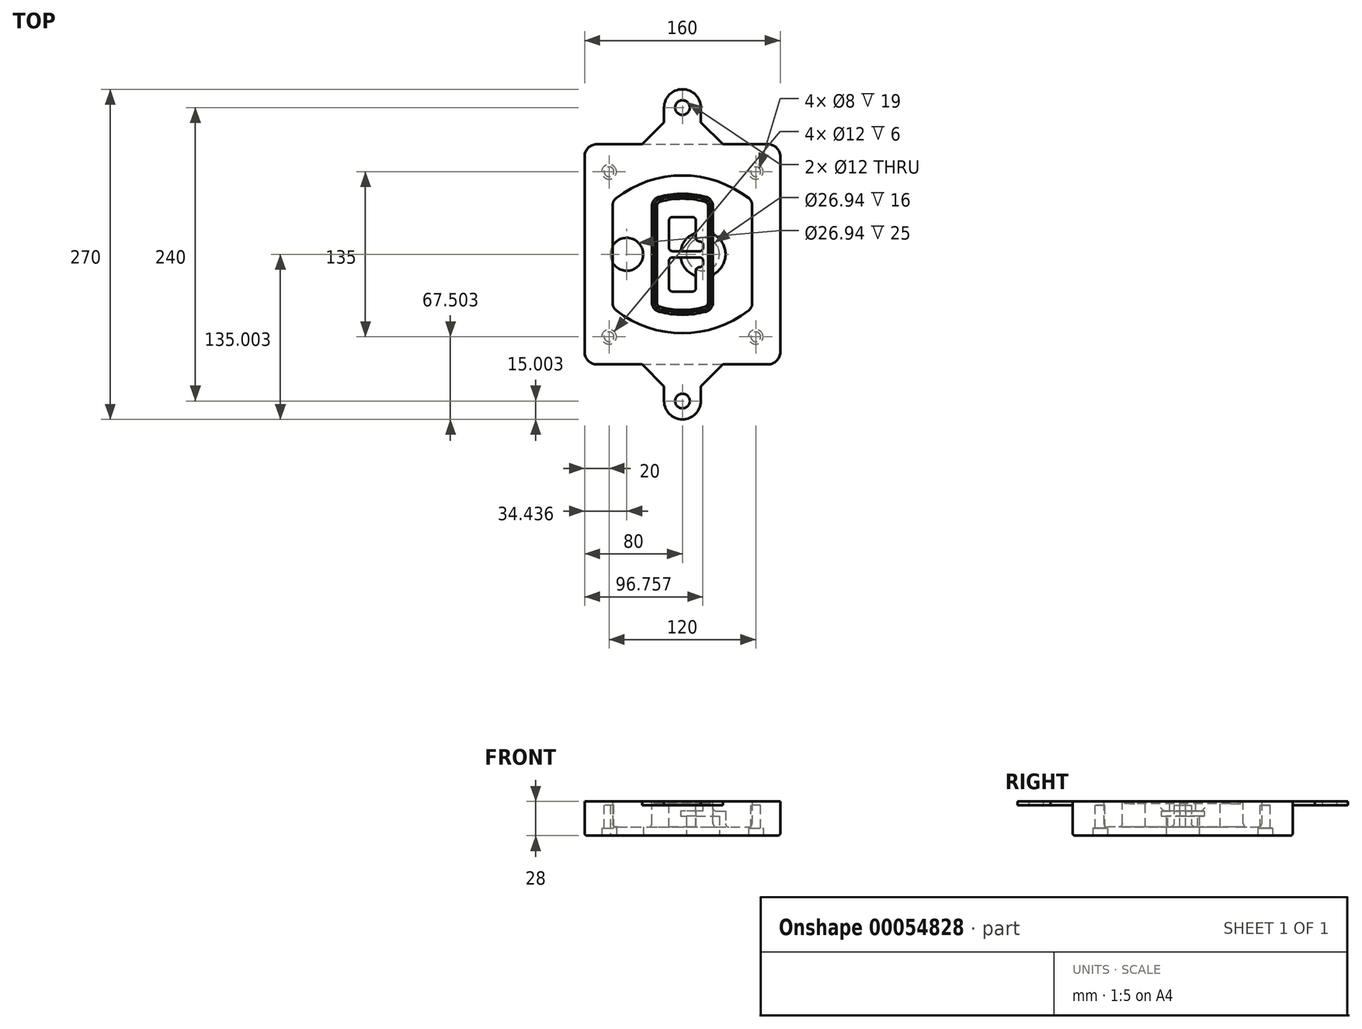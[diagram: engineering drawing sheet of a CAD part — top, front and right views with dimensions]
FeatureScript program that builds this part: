
annotation { "Feature Type Name" : "Feature", "Feature Type Description" : "" }
export const myFeature = defineFeature(function(context is Context, id is Id, definition is map)
    precondition{}
    {
        {
            var Q0;
            Q0=qCreatedBy(makeId("Top.planeOp"),FACE);
            var sketch = newSketch(context, id + "F0", { "sketchPlane" : qUnion([Q0])});
            skPoint(sketch, "E0.rect.middle", {"position": v(0, 0) * mm});
            skLineSegment(sketch, "E1.bottom", {"start": v(24.05, 28.38) * mm, "end": v(164.05, 28.38) * mm});
            skLineSegment(sketch, "E1.top", {"start": v(24.05, 208.38) * mm, "end": v(164.05, 208.38) * mm});
            skLineSegment(sketch, "E1.left", {"start": v(14.05, 38.38) * mm, "end": v(14.05, 198.38) * mm});
            skLineSegment(sketch, "E1.right", {"start": v(174.05, 38.38) * mm, "end": v(174.05, 198.38) * mm});
            skLineSegment(sketch, "E2", {"start": v(14.05, 208.38) * mm, "end": v(174.05, 28.38) * mm, "construction": true});
            skLineSegment(sketch, "E3", {"start": v(174.05, 208.38) * mm, "end": v(14.05, 28.38) * mm, "construction": true});
            skCircle(sketch, "E4", {"center": v(34.05, 185.88) * mm, "radius": 4 * mm});
            skCircle(sketch, "E5", {"center": v(154.05, 185.88) * mm, "radius": 4 * mm});
            skCircle(sketch, "E6", {"center": v(154.05, 50.88) * mm, "radius": 4 * mm});
            skCircle(sketch, "E7", {"center": v(34.05, 50.88) * mm, "radius": 4 * mm});
            skLineSegment(sketch, "E8", {"start": v(34.05, 185.88) * mm, "end": v(154.05, 185.88) * mm, "construction": true});
            skLineSegment(sketch, "E9", {"start": v(154.05, 185.88) * mm, "end": v(154.05, 50.88) * mm, "construction": true});
            skLineSegment(sketch, "E10", {"start": v(154.05, 50.88) * mm, "end": v(34.05, 50.88) * mm, "construction": true});
            skLineSegment(sketch, "E11", {"start": v(34.05, 50.88) * mm, "end": v(34.05, 185.88) * mm, "construction": true});
            skLineSegment(sketch, "E12", {"start": v(34.05, 158.68) * mm, "end": v(34.05, 78.09) * mm});
            skLineSegment(sketch, "E13", {"start": v(154.05, 158.68) * mm, "end": v(154.05, 78.09) * mm});
            skArc(sketch, "E14", {"start": v(150.2, 166.56) * mm, "mid": v(94.05, 185.88) * mm, "end": v(37.9, 166.56) * mm});
            skArc(sketch, "E15", {"start": v(37.9, 70.2) * mm, "mid": v(94.05, 50.88) * mm, "end": v(150.2, 70.2) * mm});
            skLineSegment(sketch, "E16", {"start": v(34.05, 118.38) * mm, "end": v(154.05, 118.38) * mm, "construction": true});
            skPoint(sketch, "E17.visualSharp", {"position": v(34.05, 73.38) * mm});
            skArc(sketch, "E17.filletArc", {"start": v(34.05, 78.09) * mm, "mid": v(35.06, 73.7) * mm, "end": v(37.9, 70.2) * mm});
            skPoint(sketch, "E18.visualSharp", {"position": v(34.05, 163.38) * mm});
            skArc(sketch, "E18.filletArc", {"start": v(37.9, 166.56) * mm, "mid": v(35.06, 163.06) * mm, "end": v(34.05, 158.68) * mm});
            skPoint(sketch, "E19.visualSharp", {"position": v(154.05, 163.38) * mm});
            skArc(sketch, "E19.filletArc", {"start": v(154.05, 158.68) * mm, "mid": v(153.04, 163.06) * mm, "end": v(150.2, 166.56) * mm});
            skPoint(sketch, "E20.visualSharp", {"position": v(154.05, 73.38) * mm});
            skArc(sketch, "E20.filletArc", {"start": v(150.2, 70.2) * mm, "mid": v(153.04, 73.7) * mm, "end": v(154.05, 78.09) * mm});
            skPoint(sketch, "E21.visualSharp", {"position": v(14.05, 208.38) * mm});
            skArc(sketch, "E21.filletArc", {"start": v(24.05, 208.38) * mm, "mid": v(16.98, 205.45) * mm, "end": v(14.05, 198.38) * mm});
            skPoint(sketch, "E22.visualSharp", {"position": v(174.05, 208.38) * mm});
            skArc(sketch, "E22.filletArc", {"start": v(174.05, 198.38) * mm, "mid": v(171.12, 205.45) * mm, "end": v(164.05, 208.38) * mm});
            skPoint(sketch, "E23.visualSharp", {"position": v(174.05, 28.38) * mm});
            skArc(sketch, "E23.filletArc", {"start": v(164.05, 28.38) * mm, "mid": v(171.12, 31.31) * mm, "end": v(174.05, 38.38) * mm});
            skPoint(sketch, "E24.visualSharp", {"position": v(14.05, 28.38) * mm});
            skArc(sketch, "E24.filletArc", {"start": v(14.05, 38.38) * mm, "mid": v(16.98, 31.31) * mm, "end": v(24.05, 28.38) * mm});
            skArc(sketch, "E25.0", {"start": v(151.05, 158.68) * mm, "mid": v(150.34, 161.75) * mm, "end": v(148.36, 164.2) * mm});
            skLineSegment(sketch, "E25.1", {"start": v(151.05, 158.68) * mm, "end": v(151.05, 78.09) * mm});
            skArc(sketch, "E25.2", {"start": v(148.36, 72.57) * mm, "mid": v(150.34, 75.02) * mm, "end": v(151.05, 78.09) * mm});
            skArc(sketch, "E25.3", {"start": v(39.74, 72.57) * mm, "mid": v(94.05, 53.88) * mm, "end": v(148.36, 72.57) * mm});
            skArc(sketch, "E25.4", {"start": v(37.05, 78.09) * mm, "mid": v(37.76, 75.02) * mm, "end": v(39.74, 72.57) * mm});
            skArc(sketch, "E25.5", {"start": v(148.36, 164.2) * mm, "mid": v(94.05, 182.88) * mm, "end": v(39.74, 164.2) * mm});
            skLineSegment(sketch, "E25.6", {"start": v(37.05, 158.68) * mm, "end": v(37.05, 78.09) * mm});
            skArc(sketch, "E25.7", {"start": v(39.74, 164.2) * mm, "mid": v(37.76, 161.75) * mm, "end": v(37.05, 158.68) * mm});
            skArc(sketch, "E26.0", {"start": v(35.43, 169.71) * mm, "mid": v(31.47, 164.82) * mm, "end": v(30.05, 158.68) * mm});
            skArc(sketch, "E26.1", {"start": v(152.67, 169.71) * mm, "mid": v(94.05, 189.88) * mm, "end": v(35.43, 169.71) * mm});
            skArc(sketch, "E26.2", {"start": v(158.05, 158.68) * mm, "mid": v(156.63, 164.82) * mm, "end": v(152.67, 169.71) * mm});
            skLineSegment(sketch, "E26.3", {"start": v(158.05, 158.68) * mm, "end": v(158.05, 78.09) * mm});
            skArc(sketch, "E26.4", {"start": v(152.67, 67.05) * mm, "mid": v(156.63, 71.95) * mm, "end": v(158.05, 78.09) * mm});
            skLineSegment(sketch, "E26.5", {"start": v(30.05, 158.68) * mm, "end": v(30.05, 78.09) * mm});
            skArc(sketch, "E26.6", {"start": v(35.43, 67.05) * mm, "mid": v(94.05, 46.88) * mm, "end": v(152.67, 67.05) * mm});
            skArc(sketch, "E26.7", {"start": v(30.05, 78.09) * mm, "mid": v(31.47, 71.95) * mm, "end": v(35.43, 67.05) * mm});
            skSolve(sketch);
        }
        {
            var Q0;
            Q0=makeQuery(id+"F0.imprint","IMPRINT",FACE,{"disambiguationData":[TD([[makeQuery(id+"F0.imprint","IMPRINT",EDGE,{"derivedFrom":sQuery(id+"F0.wireOp",EDGE,"E1.bottom")}),1.0]])]});
            var Q1;
            Q1=makeQuery(id+"F0.imprint","IMPRINT",FACE,{"disambiguationData":[TD([[makeQuery(id+"F0.imprint","IMPRINT",EDGE,{"derivedFrom":sQuery(id+"F0.wireOp",EDGE,"E12")}),1.0]])]});
            var Q2;
            Q2=makeQuery(id+"F0.imprint","IMPRINT",FACE,{"disambiguationData":[TD([[makeQuery(id+"F0.imprint","IMPRINT",EDGE,{"derivedFrom":sQuery(id+"F0.wireOp",EDGE,"E25.0")}),1.0]])]});
            var Q3;
            Q3=makeQuery(id+"F0.imprint","IMPRINT",FACE,{"disambiguationData":[TD([[makeQuery(id+"F0.imprint","IMPRINT",EDGE,{"derivedFrom":sQuery(id+"F0.wireOp",EDGE,"E12")}),-1.0]])]});
            extrude(context, id + "F1", {"entities" : qUnion([Q0, Q1, Q2, Q3]), "oppositeDirection" : true, "depth" : 25 * mm});
        }
        {
            var Q0;
            Q0=makeQuery(id+"F0.imprint","IMPRINT",FACE,{"disambiguationData":[TD([[makeQuery(id+"F0.imprint","IMPRINT",EDGE,{"derivedFrom":sQuery(id+"F0.wireOp",EDGE,"E12")}),1.0]])]});
            extrude(context, id + "F2", {"entities" : qUnion([Q0]), "operationType" : NewBodyOperationType.ADD, "depth" : 3 * mm});
        }
        {
            var Q0;
            Q0=makeQuery(id+"F0.imprint","IMPRINT",FACE,{"disambiguationData":[TD([[makeQuery(id+"F0.imprint","IMPRINT",EDGE,{"derivedFrom":sQuery(id+"F0.wireOp",EDGE,"E25.0")}),1.0]])]});
            extrude(context, id + "F3", {"entities" : qUnion([Q0]), "operationType" : NewBodyOperationType.REMOVE, "oppositeDirection" : true, "depth" : 18 * mm});
        }
        {
            var Q0;
            Q0=makeQuery(id+"F2.opExtrude","CAP_FACE",FACE,{"disambiguationData":[OSD([sQuery(id+"F0.wireOp",EDGE,"E12"),sQuery(id+"F0.wireOp",EDGE,"E13"),sQuery(id+"F0.wireOp",EDGE,"E14"),sQuery(id+"F0.wireOp",EDGE,"E15"),sQuery(id+"F0.wireOp",EDGE,"E17.filletArc"),sQuery(id+"F0.wireOp",EDGE,"E18.filletArc"),sQuery(id+"F0.wireOp",EDGE,"E19.filletArc"),sQuery(id+"F0.wireOp",EDGE,"E20.filletArc"),sQuery(id+"F0.wireOp",EDGE,"E25.0"),sQuery(id+"F0.wireOp",EDGE,"E25.1"),sQuery(id+"F0.wireOp",EDGE,"E25.2"),sQuery(id+"F0.wireOp",EDGE,"E25.3"),sQuery(id+"F0.wireOp",EDGE,"E25.4"),sQuery(id+"F0.wireOp",EDGE,"E25.5"),sQuery(id+"F0.wireOp",EDGE,"E25.6"),sQuery(id+"F0.wireOp",EDGE,"E25.7")])],"isStart":false});
            var sketch = newSketch(context, id + "F4", { "sketchPlane" : qUnion([Q0])});
            skArc(sketch, "E27.0", {"start": v(74.97, 71.41) * mm, "mid": v(94.05, 68.88) * mm, "end": v(113.13, 71.41) * mm});
            skArc(sketch, "E28.0", {"start": v(113.13, 165.35) * mm, "mid": v(94.05, 167.88) * mm, "end": v(74.97, 165.35) * mm});
            skLineSegment(sketch, "E29", {"start": v(69.05, 157.63) * mm, "end": v(69.05, 79.14) * mm});
            skLineSegment(sketch, "E30", {"start": v(119.05, 157.63) * mm, "end": v(119.05, 79.14) * mm});
            skLineSegment(sketch, "E31", {"start": v(69.05, 163.48) * mm, "end": v(119.05, 163.48) * mm, "construction": true});
            skLineSegment(sketch, "E32", {"start": v(69.05, 73.28) * mm, "end": v(119.05, 73.28) * mm, "construction": true});
            skPoint(sketch, "E33.visualSharp", {"position": v(69.05, 163.48) * mm});
            skArc(sketch, "E33.filletArc", {"start": v(74.97, 165.35) * mm, "mid": v(70.7, 162.5) * mm, "end": v(69.05, 157.63) * mm});
            skPoint(sketch, "E34.visualSharp", {"position": v(119.05, 163.48) * mm});
            skArc(sketch, "E34.filletArc", {"start": v(119.05, 157.63) * mm, "mid": v(117.4, 162.5) * mm, "end": v(113.13, 165.35) * mm});
            skPoint(sketch, "E35.visualSharp", {"position": v(119.05, 73.28) * mm});
            skArc(sketch, "E35.filletArc", {"start": v(113.13, 71.41) * mm, "mid": v(117.4, 74.27) * mm, "end": v(119.05, 79.14) * mm});
            skPoint(sketch, "E36.visualSharp", {"position": v(69.05, 73.28) * mm});
            skArc(sketch, "E36.filletArc", {"start": v(69.05, 79.14) * mm, "mid": v(70.7, 74.27) * mm, "end": v(74.97, 71.41) * mm});
            skArc(sketch, "E37.0", {"start": v(148.36, 164.2) * mm, "mid": v(94.05, 182.88) * mm, "end": v(39.74, 164.2) * mm});
            skArc(sketch, "E37.1", {"start": v(39.74, 164.2) * mm, "mid": v(37.76, 161.75) * mm, "end": v(37.05, 158.68) * mm});
            skLineSegment(sketch, "E37.2", {"start": v(37.05, 158.68) * mm, "end": v(37.05, 78.09) * mm});
            skArc(sketch, "E37.3", {"start": v(37.05, 78.09) * mm, "mid": v(37.76, 75.02) * mm, "end": v(39.74, 72.57) * mm});
            skArc(sketch, "E37.4", {"start": v(39.74, 72.57) * mm, "mid": v(94.05, 53.88) * mm, "end": v(148.36, 72.57) * mm});
            skArc(sketch, "E37.5", {"start": v(148.36, 72.57) * mm, "mid": v(150.34, 75.02) * mm, "end": v(151.05, 78.09) * mm});
            skLineSegment(sketch, "E37.6", {"start": v(151.05, 158.68) * mm, "end": v(151.05, 78.09) * mm});
            skArc(sketch, "E37.7", {"start": v(151.05, 158.68) * mm, "mid": v(150.34, 161.75) * mm, "end": v(148.36, 164.2) * mm});
            skLineSegment(sketch, "E38.0", {"start": v(117.05, 157.63) * mm, "end": v(117.05, 79.14) * mm});
            skArc(sketch, "E38.1", {"start": v(112.61, 73.34) * mm, "mid": v(115.81, 75.49) * mm, "end": v(117.05, 79.14) * mm});
            skArc(sketch, "E38.2", {"start": v(75.49, 73.34) * mm, "mid": v(94.05, 70.88) * mm, "end": v(112.61, 73.34) * mm});
            skArc(sketch, "E38.3", {"start": v(71.05, 79.14) * mm, "mid": v(72.29, 75.49) * mm, "end": v(75.49, 73.34) * mm});
            skLineSegment(sketch, "E38.4", {"start": v(71.05, 157.63) * mm, "end": v(71.05, 79.14) * mm});
            skArc(sketch, "E38.5", {"start": v(117.05, 157.63) * mm, "mid": v(115.81, 161.28) * mm, "end": v(112.61, 163.42) * mm});
            skArc(sketch, "E38.6", {"start": v(75.49, 163.42) * mm, "mid": v(72.29, 161.28) * mm, "end": v(71.05, 157.63) * mm});
            skArc(sketch, "E38.7", {"start": v(112.61, 163.42) * mm, "mid": v(94.05, 165.88) * mm, "end": v(75.49, 163.42) * mm});
            skArc(sketch, "E39.0", {"start": v(115.05, 157.63) * mm, "mid": v(114.23, 160.06) * mm, "end": v(112.1, 161.5) * mm});
            skLineSegment(sketch, "E39.1", {"start": v(115.05, 157.63) * mm, "end": v(115.05, 79.14) * mm});
            skArc(sketch, "E39.2", {"start": v(112.1, 75.27) * mm, "mid": v(114.23, 76.7) * mm, "end": v(115.05, 79.14) * mm});
            skArc(sketch, "E39.3", {"start": v(76, 75.27) * mm, "mid": v(94.05, 72.88) * mm, "end": v(112.1, 75.27) * mm});
            skArc(sketch, "E39.4", {"start": v(73.05, 79.14) * mm, "mid": v(73.87, 76.7) * mm, "end": v(76, 75.27) * mm});
            skArc(sketch, "E39.5", {"start": v(112.1, 161.5) * mm, "mid": v(94.05, 163.88) * mm, "end": v(76, 161.5) * mm});
            skLineSegment(sketch, "E39.6", {"start": v(73.05, 157.63) * mm, "end": v(73.05, 79.14) * mm});
            skArc(sketch, "E39.7", {"start": v(76, 161.5) * mm, "mid": v(73.87, 160.06) * mm, "end": v(73.05, 157.63) * mm});
            skLineSegment(sketch, "E40", {"start": v(69.05, 118.38) * mm, "end": v(119.05, 118.38) * mm, "construction": true});
            skLineSegment(sketch, "E41", {"start": v(83.05, 123.88) * mm, "end": v(83.05, 145.88) * mm});
            skLineSegment(sketch, "E42", {"start": v(86.05, 148.88) * mm, "end": v(102.05, 148.88) * mm});
            skLineSegment(sketch, "E43", {"start": v(105.05, 145.88) * mm, "end": v(105.05, 131.88) * mm});
            skLineSegment(sketch, "E44", {"start": v(108.05, 128.88) * mm, "end": v(108.05, 128.88) * mm});
            skLineSegment(sketch, "E45", {"start": v(111.05, 125.88) * mm, "end": v(111.05, 123.88) * mm});
            skLineSegment(sketch, "E46", {"start": v(108.05, 120.88) * mm, "end": v(86.05, 120.88) * mm});
            skPoint(sketch, "E47.visualSharp", {"position": v(83.05, 148.88) * mm});
            skArc(sketch, "E47.filletArc", {"start": v(86.05, 148.88) * mm, "mid": v(83.93, 148) * mm, "end": v(83.05, 145.88) * mm});
            skPoint(sketch, "E48.visualSharp", {"position": v(105.05, 148.88) * mm});
            skArc(sketch, "E48.filletArc", {"start": v(105.05, 145.88) * mm, "mid": v(104.17, 148) * mm, "end": v(102.05, 148.88) * mm});
            skPoint(sketch, "E49.visualSharp", {"position": v(105.05, 128.88) * mm});
            skArc(sketch, "E49.filletArc", {"start": v(105.05, 131.88) * mm, "mid": v(105.93, 129.76) * mm, "end": v(108.05, 128.88) * mm});
            skPoint(sketch, "E50.visualSharp", {"position": v(111.05, 128.88) * mm});
            skArc(sketch, "E50.filletArc", {"start": v(111.05, 125.88) * mm, "mid": v(110.17, 128) * mm, "end": v(108.05, 128.88) * mm});
            skPoint(sketch, "E51.visualSharp", {"position": v(111.05, 120.88) * mm});
            skArc(sketch, "E51.filletArc", {"start": v(108.05, 120.88) * mm, "mid": v(110.17, 121.76) * mm, "end": v(111.05, 123.88) * mm});
            skPoint(sketch, "E52.visualSharp", {"position": v(83.05, 120.88) * mm});
            skArc(sketch, "E52.filletArc", {"start": v(83.05, 123.88) * mm, "mid": v(83.93, 121.76) * mm, "end": v(86.05, 120.88) * mm});
            skLineSegment(sketch, "E53.0.MirrorCS", {"start": v(108.05, 115.88) * mm, "end": v(86.05, 115.88) * mm});
            skArc(sketch, "E54.0.MirrorCS", {"start": v(83.05, 112.88) * mm, "mid": v(83.93, 115) * mm, "end": v(86.05, 115.88) * mm});
            skLineSegment(sketch, "E55.0.MirrorCS", {"start": v(83.05, 112.88) * mm, "end": v(83.05, 90.88) * mm});
            skArc(sketch, "E56.0.MirrorCS", {"start": v(86.05, 87.88) * mm, "mid": v(83.93, 88.76) * mm, "end": v(83.05, 90.88) * mm});
            skLineSegment(sketch, "E57.0.MirrorCS", {"start": v(86.05, 87.88) * mm, "end": v(102.05, 87.88) * mm});
            skArc(sketch, "E58.0.MirrorCS", {"start": v(105.05, 90.88) * mm, "mid": v(104.17, 88.76) * mm, "end": v(102.05, 87.88) * mm});
            skLineSegment(sketch, "E59.0.MirrorCS", {"start": v(105.05, 90.88) * mm, "end": v(105.05, 104.88) * mm});
            skArc(sketch, "E60.0.MirrorCS", {"start": v(105.05, 104.88) * mm, "mid": v(105.93, 107) * mm, "end": v(108.05, 107.88) * mm});
            skArc(sketch, "E61.0.MirrorCS", {"start": v(111.05, 110.88) * mm, "mid": v(110.17, 108.76) * mm, "end": v(108.05, 107.88) * mm});
            skLineSegment(sketch, "E62.0.MirrorCS", {"start": v(111.05, 110.88) * mm, "end": v(111.05, 112.88) * mm});
            skArc(sketch, "E63.0.MirrorCS", {"start": v(108.05, 115.88) * mm, "mid": v(110.17, 115) * mm, "end": v(111.05, 112.88) * mm});
            skSolve(sketch);
        }
        {
            var Q0;
            Q0=makeQuery(id+"F4.imprint","IMPRINT",FACE,{"disambiguationData":[TD([[makeQuery(id+"F4.imprint","IMPRINT",EDGE,{"derivedFrom":sQuery(id+"F4.wireOp",EDGE,"E27.0")}),1.0]])]});
            var Q1;
            Q1=makeQuery(id+"F4.imprint","IMPRINT",FACE,{"disambiguationData":[TD([[makeQuery(id+"F4.imprint","IMPRINT",EDGE,{"derivedFrom":sQuery(id+"F4.wireOp",EDGE,"E38.0")}),-1.0]])]});
            var Q2;
            Q2=makeQuery(id+"F4.imprint","IMPRINT",FACE,{"disambiguationData":[TD([[makeQuery(id+"F4.imprint","IMPRINT",EDGE,{"derivedFrom":sQuery(id+"F4.wireOp",EDGE,"E39.0")}),1.0]])]});
            extrude(context, id + "F5", {"entities" : qUnion([Q0, Q1, Q2]), "operationType" : NewBodyOperationType.ADD, "endBound" : BoundingType.UP_TO_NEXT, "oppositeDirection" : true, "depth" : 25 * mm});
        }
        {
            var Q0;
            Q0=makeQuery(id+"F4.imprint","IMPRINT",FACE,{"disambiguationData":[TD([[makeQuery(id+"F4.imprint","IMPRINT",EDGE,{"derivedFrom":sQuery(id+"F4.wireOp",EDGE,"E38.0")}),-1.0]])]});
            extrude(context, id + "F6", {"entities" : qUnion([Q0]), "operationType" : NewBodyOperationType.REMOVE, "oppositeDirection" : true, "depth" : 2 * mm});
        }
        {
            var Q0;
            Q0=makeQuery(id+"F1.opExtrude","CAP_FACE",FACE,{"disambiguationData":[OSD([sQuery(id+"F0.wireOp",EDGE,"E1.bottom"),sQuery(id+"F0.wireOp",EDGE,"E1.top"),sQuery(id+"F0.wireOp",EDGE,"E1.left"),sQuery(id+"F0.wireOp",EDGE,"E1.right"),sQuery(id+"F0.wireOp",EDGE,"E4"),sQuery(id+"F0.wireOp",EDGE,"E5"),sQuery(id+"F0.wireOp",EDGE,"E6"),sQuery(id+"F0.wireOp",EDGE,"E7"),sQuery(id+"F0.wireOp",EDGE,"E21.filletArc"),sQuery(id+"F0.wireOp",EDGE,"E22.filletArc"),sQuery(id+"F0.wireOp",EDGE,"E23.filletArc"),sQuery(id+"F0.wireOp",EDGE,"E24.filletArc")])],"isStart":false});
            var sketch = newSketch(context, id + "F7", { "sketchPlane" : qUnion([Q0])});
            skCircle(sketch, "E64", {"center": v(110.8, -118.38) * mm, "radius": 13.47 * mm});
            skCircle(sketch, "E65", {"center": v(48.49, -118.38) * mm, "radius": 13.47 * mm});
            skLineSegment(sketch, "E66", {"start": v(174.05, -118.38) * mm, "end": v(14.05, -118.38) * mm});
            skCircle(sketch, "E67", {"center": v(110.8, -118.38) * mm, "radius": 18.47 * mm});
            skCircle(sketch, "E68", {"center": v(154.05, -185.88) * mm, "radius": 6 * mm});
            skCircle(sketch, "E69", {"center": v(34.05, -185.88) * mm, "radius": 6 * mm});
            skCircle(sketch, "E70", {"center": v(34.05, -50.88) * mm, "radius": 6 * mm});
            skCircle(sketch, "E71", {"center": v(154.05, -50.88) * mm, "radius": 6 * mm});
            skSolve(sketch);
        }
        {
            var Q0;
            {var subQ1=sQuery(id+"F7.wireOp",EDGE,"E66");var subQ4=sQuery(id+"F7.wireOp",EDGE,"E64");var subQ6=makeQuery(id+"F7.imprint","INTERSECT",VERTEX,{"disambiguationData":[OD(0.0)],"derivedFrom":[subQ4,subQ1]});Q0=makeQuery(id+"F7.imprint","IMPRINT",FACE,{"disambiguationData":[TD([[makeQuery(id+"F7.imprint","IMPRINT",EDGE,{"disambiguationData":[TD([[subQ6,-1.0]])],"derivedFrom":subQ4}),-1.0]])]});}
            var Q1;
            {var subQ0=sQuery(id+"F7.wireOp",EDGE,"E66");var subQ1=sQuery(id+"F7.wireOp",EDGE,"E64");var subQ3=makeQuery(id+"F7.imprint","INTERSECT",VERTEX,{"disambiguationData":[OD(0.0)],"derivedFrom":[subQ1,subQ0]});Q1=makeQuery(id+"F7.imprint","IMPRINT",FACE,{"disambiguationData":[TD([[makeQuery(id+"F7.imprint","IMPRINT",EDGE,{"disambiguationData":[TD([[subQ3,-1.0]])],"derivedFrom":subQ1}),1.0]])]});}
            var Q2;
            {var subQ0=sQuery(id+"F7.wireOp",EDGE,"E66");var subQ1=sQuery(id+"F7.wireOp",EDGE,"E64");var subQ3=makeQuery(id+"F7.imprint","INTERSECT",VERTEX,{"disambiguationData":[OD(0.0)],"derivedFrom":[subQ1,subQ0]});Q2=makeQuery(id+"F7.imprint","IMPRINT",FACE,{"disambiguationData":[TD([[makeQuery(id+"F7.imprint","IMPRINT",EDGE,{"disambiguationData":[TD([[subQ3,1.0]])],"derivedFrom":subQ1}),1.0]])]});}
            var Q3;
            {var subQ1=sQuery(id+"F7.wireOp",EDGE,"E66");var subQ4=sQuery(id+"F7.wireOp",EDGE,"E64");var subQ6=makeQuery(id+"F7.imprint","INTERSECT",VERTEX,{"disambiguationData":[OD(0.0)],"derivedFrom":[subQ4,subQ1]});Q3=makeQuery(id+"F7.imprint","IMPRINT",FACE,{"disambiguationData":[TD([[makeQuery(id+"F7.imprint","IMPRINT",EDGE,{"disambiguationData":[TD([[subQ6,1.0]])],"derivedFrom":subQ4}),-1.0]])]});}
            extrude(context, id + "F8", {"entities" : qUnion([Q0, Q1, Q2, Q3]), "operationType" : NewBodyOperationType.ADD, "oppositeDirection" : true, "depth" : 20 * mm});
        }
        {
            var Q0;
            {var subQ0=sQuery(id+"F7.wireOp",EDGE,"E66");var subQ1=sQuery(id+"F7.wireOp",EDGE,"E64");var subQ3=makeQuery(id+"F7.imprint","INTERSECT",VERTEX,{"disambiguationData":[OD(0.0)],"derivedFrom":[subQ1,subQ0]});Q0=makeQuery(id+"F7.imprint","IMPRINT",FACE,{"disambiguationData":[TD([[makeQuery(id+"F7.imprint","IMPRINT",EDGE,{"disambiguationData":[TD([[subQ3,-1.0]])],"derivedFrom":subQ1}),1.0]])]});}
            var Q1;
            {var subQ0=sQuery(id+"F7.wireOp",EDGE,"E66");var subQ1=sQuery(id+"F7.wireOp",EDGE,"E64");var subQ3=makeQuery(id+"F7.imprint","INTERSECT",VERTEX,{"disambiguationData":[OD(0.0)],"derivedFrom":[subQ1,subQ0]});Q1=makeQuery(id+"F7.imprint","IMPRINT",FACE,{"disambiguationData":[TD([[makeQuery(id+"F7.imprint","IMPRINT",EDGE,{"disambiguationData":[TD([[subQ3,1.0]])],"derivedFrom":subQ1}),1.0]])]});}
            extrude(context, id + "F9", {"entities" : qUnion([Q0, Q1]), "operationType" : NewBodyOperationType.REMOVE, "oppositeDirection" : true, "depth" : 16 * mm});
        }
        {
            var Q0;
            {var subQ0=sQuery(id+"F7.wireOp",EDGE,"E66");var subQ1=sQuery(id+"F7.wireOp",EDGE,"E65");var subQ3=makeQuery(id+"F7.imprint","INTERSECT",VERTEX,{"disambiguationData":[OD(0.0)],"derivedFrom":[subQ1,subQ0]});Q0=makeQuery(id+"F7.imprint","IMPRINT",FACE,{"disambiguationData":[TD([[makeQuery(id+"F7.imprint","IMPRINT",EDGE,{"disambiguationData":[TD([[subQ3,-1.0]])],"derivedFrom":subQ1}),1.0]])]});}
            var Q1;
            {var subQ0=sQuery(id+"F7.wireOp",EDGE,"E66");var subQ1=sQuery(id+"F7.wireOp",EDGE,"E65");var subQ3=makeQuery(id+"F7.imprint","INTERSECT",VERTEX,{"disambiguationData":[OD(0.0)],"derivedFrom":[subQ1,subQ0]});Q1=makeQuery(id+"F7.imprint","IMPRINT",FACE,{"disambiguationData":[TD([[makeQuery(id+"F7.imprint","IMPRINT",EDGE,{"disambiguationData":[TD([[subQ3,1.0]])],"derivedFrom":subQ1}),1.0]])]});}
            extrude(context, id + "F10", {"entities" : qUnion([Q0, Q1]), "operationType" : NewBodyOperationType.REMOVE, "oppositeDirection" : true, "depth" : 25 * mm});
        }
        {
            var Q0;
            Q0=makeQuery(id+"F7.imprint","IMPRINT",FACE,{"disambiguationData":[TD([[makeQuery(id+"F7.imprint","IMPRINT",EDGE,{"derivedFrom":sQuery(id+"F7.wireOp",EDGE,"E68")}),1.0]])]});
            var Q1;
            Q1=makeQuery(id+"F7.imprint","IMPRINT",FACE,{"disambiguationData":[TD([[makeQuery(id+"F7.imprint","IMPRINT",EDGE,{"derivedFrom":makeQuery(id+"F1.opExtrude","CAP_EDGE",EDGE,{"disambiguationData":[OSD([sQuery(id+"F0.wireOp",EDGE,"E5")])],"isStart":false})}),-1.0]])]});
            var Q2;
            Q2=makeQuery(id+"F7.imprint","IMPRINT",FACE,{"disambiguationData":[TD([[makeQuery(id+"F7.imprint","IMPRINT",EDGE,{"derivedFrom":sQuery(id+"F7.wireOp",EDGE,"E69")}),1.0]])]});
            var Q3;
            Q3=makeQuery(id+"F7.imprint","IMPRINT",FACE,{"disambiguationData":[TD([[makeQuery(id+"F7.imprint","IMPRINT",EDGE,{"derivedFrom":makeQuery(id+"F1.opExtrude","CAP_EDGE",EDGE,{"disambiguationData":[OSD([sQuery(id+"F0.wireOp",EDGE,"E4")])],"isStart":false})}),-1.0]])]});
            var Q4;
            Q4=makeQuery(id+"F7.imprint","IMPRINT",FACE,{"disambiguationData":[TD([[makeQuery(id+"F7.imprint","IMPRINT",EDGE,{"derivedFrom":sQuery(id+"F7.wireOp",EDGE,"E70")}),1.0]])]});
            var Q5;
            Q5=makeQuery(id+"F7.imprint","IMPRINT",FACE,{"disambiguationData":[TD([[makeQuery(id+"F7.imprint","IMPRINT",EDGE,{"derivedFrom":makeQuery(id+"F1.opExtrude","CAP_EDGE",EDGE,{"disambiguationData":[OSD([sQuery(id+"F0.wireOp",EDGE,"E7")])],"isStart":false})}),-1.0]])]});
            var Q6;
            Q6=makeQuery(id+"F7.imprint","IMPRINT",FACE,{"disambiguationData":[TD([[makeQuery(id+"F7.imprint","IMPRINT",EDGE,{"derivedFrom":sQuery(id+"F7.wireOp",EDGE,"E71")}),1.0]])]});
            var Q7;
            Q7=makeQuery(id+"F7.imprint","IMPRINT",FACE,{"disambiguationData":[TD([[makeQuery(id+"F7.imprint","IMPRINT",EDGE,{"derivedFrom":makeQuery(id+"F1.opExtrude","CAP_EDGE",EDGE,{"disambiguationData":[OSD([sQuery(id+"F0.wireOp",EDGE,"E6")])],"isStart":false})}),-1.0]])]});
            extrude(context, id + "F11", {"entities" : qUnion([Q0, Q1, Q2, Q3, Q4, Q5, Q6, Q7]), "operationType" : NewBodyOperationType.REMOVE, "oppositeDirection" : true, "depth" : 6 * mm});
        }
        {
            var Q0;
            Q0=makeQuery(id+"F9.boolean.opBoolean","COPY",FACE,{"derivedFrom":makeQuery(id+"F9.opExtrude","CAP_FACE",FACE,{"disambiguationData":[OSD([sQuery(id+"F7.wireOp",EDGE,"E64")])],"isStart":false})});
            var sketch = newSketch(context, id + "F12", { "sketchPlane" : qUnion([Q0])});
            skArc(sketch, "E72.0", {"start": v(105.05, -100.83) * mm, "mid": v(96.62, -106.56) * mm, "end": v(92.5, -115.88) * mm});
            skArc(sketch, "E72.1", {"start": v(92.5, -120.88) * mm, "mid": v(96.62, -130.2) * mm, "end": v(105.05, -135.93) * mm});
            skLineSegment(sketch, "E73", {"start": v(92.5, -120.88) * mm, "end": v(108.05, -120.88) * mm});
            skLineSegment(sketch, "E74.0", {"start": v(108.05, -115.88) * mm, "end": v(92.5, -115.88) * mm});
            skArc(sketch, "E74.1", {"start": v(108.05, -115.88) * mm, "mid": v(110.17, -115) * mm, "end": v(111.05, -112.88) * mm});
            skLineSegment(sketch, "E74.2", {"start": v(111.05, -110.88) * mm, "end": v(111.05, -112.88) * mm});
            skArc(sketch, "E74.3", {"start": v(111.05, -110.88) * mm, "mid": v(110.17, -108.76) * mm, "end": v(108.05, -107.88) * mm});
            skArc(sketch, "E74.4", {"start": v(105.05, -104.88) * mm, "mid": v(105.93, -107) * mm, "end": v(108.05, -107.88) * mm});
            skLineSegment(sketch, "E74.5", {"start": v(105.05, -100.83) * mm, "end": v(105.05, -104.88) * mm});
            skLineSegment(sketch, "E74.7", {"start": v(108.05, -120.88) * mm, "end": v(92.5, -120.88) * mm});
            skArc(sketch, "E74.8", {"start": v(108.05, -120.88) * mm, "mid": v(110.17, -121.76) * mm, "end": v(111.05, -123.88) * mm});
            skLineSegment(sketch, "E74.9", {"start": v(111.05, -125.88) * mm, "end": v(111.05, -123.88) * mm});
            skArc(sketch, "E74.10", {"start": v(111.05, -125.88) * mm, "mid": v(110.17, -128) * mm, "end": v(108.05, -128.88) * mm});
            skArc(sketch, "E74.11", {"start": v(105.05, -131.88) * mm, "mid": v(105.93, -129.76) * mm, "end": v(108.05, -128.88) * mm});
            skLineSegment(sketch, "E74.12", {"start": v(105.05, -135.93) * mm, "end": v(105.05, -131.88) * mm});
            skPoint(sketch, "E75.orphan", {"position": v(105.05, -145.88) * mm});
            skPoint(sketch, "E76.orphan", {"position": v(86.05, -120.88) * mm});
            skPoint(sketch, "E77.orphan", {"position": v(86.05, -115.88) * mm});
            skPoint(sketch, "E78.orphan", {"position": v(105.05, -90.88) * mm});
            skSolve(sketch);
        }
        {
            var Q0;
            {var subQ7=sQuery(id+"F12.wireOp",EDGE,"E72.0");var subQ14=sQuery(id+"F12.wireOp",EDGE,"E72.1");var subQ16=sQuery(id+"F12.wireOp",EDGE,"E74.1");var subQ18=sQuery(id+"F12.wireOp",EDGE,"E74.8");Q0=qUnion([makeQuery(id+"F12.imprint","IMPRINT",FACE,{"disambiguationData":[TD([[makeQuery(id+"F12.imprint","IMPRINT",EDGE,{"derivedFrom":subQ7}),1.0]])]}),makeQuery(id+"F12.imprint","IMPRINT",FACE,{"disambiguationData":[TD([[makeQuery(id+"F12.imprint","IMPRINT",EDGE,{"derivedFrom":subQ14}),1.0]])]}),makeQuery(id+"F12.imprint","IMPRINT",FACE,{"disambiguationData":[TD([[makeQuery(id+"F12.imprint","IMPRINT",EDGE,{"derivedFrom":subQ16}),1.0]])]}),makeQuery(id+"F12.imprint","IMPRINT",FACE,{"disambiguationData":[TD([[makeQuery(id+"F12.imprint","IMPRINT",EDGE,{"derivedFrom":subQ18}),-1.0]])]})]);}
            var Q1;
            Q1=makeQuery(id+"F5.boolean.opBoolean","SPLIT",FACE,{"disambiguationData":[TD([makeQuery(id+"F5.opExtrude","SWEPT_FACE",FACE,{"disambiguationData":[OSD([sQuery(id+"F4.wireOp",EDGE,"E41")])]})])],"derivedFrom":makeQuery(id+"F3.boolean.opBoolean","COPY",FACE,{"derivedFrom":makeQuery(id+"F3.opExtrude","CAP_FACE",FACE,{"disambiguationData":[OSD([sQuery(id+"F0.wireOp",EDGE,"E25.0"),sQuery(id+"F0.wireOp",EDGE,"E25.1"),sQuery(id+"F0.wireOp",EDGE,"E25.2"),sQuery(id+"F0.wireOp",EDGE,"E25.3"),sQuery(id+"F0.wireOp",EDGE,"E25.4"),sQuery(id+"F0.wireOp",EDGE,"E25.5"),sQuery(id+"F0.wireOp",EDGE,"E25.6"),sQuery(id+"F0.wireOp",EDGE,"E25.7")])],"isStart":false})})});
            extrude(context, id + "F13", {"entities" : qUnion([Q0]), "operationType" : NewBodyOperationType.REMOVE, "endBound" : BoundingType.UP_TO_SURFACE, "endBoundEntityFace" : qUnion([Q1]), "depth" : 25 * mm});
        }
        {
            var Q0;
            Q0=makeQuery(id+"F3.boolean.opBoolean","COPY",EDGE,{"derivedFrom":makeQuery(id+"F3.opExtrude","CAP_EDGE",EDGE,{"disambiguationData":[OSD([sQuery(id+"F0.wireOp",EDGE,"E25.6")])],"isStart":false})});
            var Q1;
            Q1=makeQuery(id+"F8.boolean.opBoolean","INTERSECT",EDGE,{"derivedFrom":[makeQuery(id+"F5.opExtrude","SWEPT_FACE",FACE,{"disambiguationData":[OSD([sQuery(id+"F4.wireOp",EDGE,"E30")])]}),makeQuery(id+"F8.opExtrude","CAP_FACE",FACE,{"disambiguationData":[OSD([sQuery(id+"F7.wireOp",EDGE,"E67")])],"isStart":false})]});
            var Q2;
            Q2=makeQuery(id+"F8.boolean.opBoolean","INTERSECT",EDGE,{"disambiguationData":[OD(1.0)],"derivedFrom":[makeQuery(id+"F5.opExtrude","SWEPT_FACE",FACE,{"disambiguationData":[OSD([sQuery(id+"F4.wireOp",EDGE,"E30")])]}),makeQuery(id+"F8.opExtrude","SWEPT_FACE",FACE,{"disambiguationData":[OSD([sQuery(id+"F7.wireOp",EDGE,"E67")])]})]});
            var Q3;
            {var subQ0=sQuery(id+"F4.wireOp",EDGE,"E30");Q3=makeQuery(id+"F8.boolean.opBoolean","SPLIT",EDGE,{"disambiguationData":[TD([makeQuery(id+"F5.opExtrude","SWEPT_FACE",FACE,{"disambiguationData":[OSD([sQuery(id+"F4.wireOp",EDGE,"E35.filletArc")])]})])],"derivedFrom":makeQuery(id+"F5.opExtrude","CAP_EDGE",EDGE,{"disambiguationData":[OSD([subQ0])],"isStart":false})});}
            var Q4;
            {var subQ0=sQuery(id+"F0.wireOp",EDGE,"E25.7");var subQ1=sQuery(id+"F0.wireOp",EDGE,"E25.1");var subQ2=sQuery(id+"F0.wireOp",EDGE,"E25.6");var subQ3=sQuery(id+"F0.wireOp",EDGE,"E25.5");var subQ4=sQuery(id+"F0.wireOp",EDGE,"E25.4");var subQ5=sQuery(id+"F0.wireOp",EDGE,"E25.0");var subQ6=sQuery(id+"F0.wireOp",EDGE,"E25.2");var subQ7=sQuery(id+"F0.wireOp",EDGE,"E25.3");Q4=makeQuery(id+"F8.boolean.opBoolean","INTERSECT",EDGE,{"derivedFrom":[makeQuery(id+"F5.boolean.opBoolean","SPLIT",FACE,{"disambiguationData":[TD([makeQuery(id+"F2.opExtrude","SWEPT_FACE",FACE,{"disambiguationData":[OSD([subQ5])]})])],"derivedFrom":makeQuery(id+"F3.boolean.opBoolean","COPY",FACE,{"derivedFrom":makeQuery(id+"F3.opExtrude","CAP_FACE",FACE,{"disambiguationData":[OSD([subQ5,subQ1,subQ6,subQ7,subQ4,subQ3,subQ2,subQ0])],"isStart":false})})}),makeQuery(id+"F8.opExtrude","SWEPT_FACE",FACE,{"disambiguationData":[OSD([sQuery(id+"F7.wireOp",EDGE,"E67")])]})]});}
            var Q5;
            Q5=makeQuery(id+"F8.boolean.opBoolean","INTERSECT",EDGE,{"disambiguationData":[OD(0.0)],"derivedFrom":[makeQuery(id+"F5.opExtrude","SWEPT_FACE",FACE,{"disambiguationData":[OSD([sQuery(id+"F4.wireOp",EDGE,"E30")])]}),makeQuery(id+"F8.opExtrude","SWEPT_FACE",FACE,{"disambiguationData":[OSD([sQuery(id+"F7.wireOp",EDGE,"E67")])]})]});
            fillet(context, id + "F14", {"entities" : qUnion([Q0, Q1, Q2, Q3, Q4, Q5]), "radius" : 3 * mm, "tangentPropagation" : true, "allowEdgeOverflow" : false});
        }
        {
            var Q0;
            Q0=makeQuery(id+"F1.opExtrude","CAP_EDGE",EDGE,{"disambiguationData":[OSD([sQuery(id+"F0.wireOp",EDGE,"E1.bottom")])],"isStart":false});
            fillet(context, id + "F15", {"entities" : qUnion([Q0]), "radius" : 2 * mm, "tangentPropagation" : true, "allowEdgeOverflow" : false});
        }
        {
            var Q0;
            {var subQ0=sQuery(id+"F0.wireOp",EDGE,"E22.filletArc");var subQ1=sQuery(id+"F0.wireOp",EDGE,"E7");var subQ2=sQuery(id+"F0.wireOp",EDGE,"E6");var subQ3=sQuery(id+"F0.wireOp",EDGE,"E5");var subQ4=sQuery(id+"F0.wireOp",EDGE,"E4");var subQ5=sQuery(id+"F0.wireOp",EDGE,"E1.bottom");var subQ6=sQuery(id+"F0.wireOp",EDGE,"E21.filletArc");var subQ7=sQuery(id+"F0.wireOp",EDGE,"E1.top");var subQ8=sQuery(id+"F0.wireOp",EDGE,"E1.left");var subQ9=sQuery(id+"F0.wireOp",EDGE,"E1.right");var subQ10=sQuery(id+"F0.wireOp",EDGE,"E23.filletArc");var subQ11=sQuery(id+"F0.wireOp",EDGE,"E24.filletArc");Q0=makeQuery(id+"F2.boolean.opBoolean","SPLIT",FACE,{"disambiguationData":[TD([makeQuery(id+"F1.opExtrude","SWEPT_FACE",FACE,{"disambiguationData":[OSD([subQ5])]})])],"derivedFrom":makeQuery(id+"F1.opExtrude","CAP_FACE",FACE,{"disambiguationData":[OSD([subQ5,subQ7,subQ8,subQ9,subQ4,subQ3,subQ2,subQ1,subQ6,subQ0,subQ10,subQ11])],"isStart":true})});}
            var sketch = newSketch(context, id + "F16", { "sketchPlane" : qUnion([Q0])});
            skLineSegment(sketch, "E79.0", {"start": v(14.05, 38.38) * mm, "end": v(14.05, 198.38) * mm});
            skArc(sketch, "E79.1", {"start": v(24.05, 208.38) * mm, "mid": v(16.98, 205.45) * mm, "end": v(14.05, 198.38) * mm});
            skLineSegment(sketch, "E79.2", {"start": v(24.05, 208.38) * mm, "end": v(164.05, 208.38) * mm});
            skArc(sketch, "E79.3", {"start": v(174.05, 198.38) * mm, "mid": v(171.12, 205.45) * mm, "end": v(164.05, 208.38) * mm});
            skLineSegment(sketch, "E79.4", {"start": v(174.05, 38.38) * mm, "end": v(174.05, 198.38) * mm});
            skArc(sketch, "E79.5", {"start": v(164.05, 28.38) * mm, "mid": v(171.12, 31.31) * mm, "end": v(174.05, 38.38) * mm});
            skLineSegment(sketch, "E79.6", {"start": v(24.05, 28.38) * mm, "end": v(164.05, 28.38) * mm});
            skArc(sketch, "E79.7", {"start": v(14.05, 38.38) * mm, "mid": v(16.98, 31.31) * mm, "end": v(24.05, 28.38) * mm});
            skLineSegment(sketch, "E79.8", {"start": v(34.05, 158.68) * mm, "end": v(34.05, 78.09) * mm});
            skArc(sketch, "E79.9", {"start": v(37.9, 166.56) * mm, "mid": v(35.06, 163.06) * mm, "end": v(34.05, 158.68) * mm});
            skArc(sketch, "E79.10", {"start": v(150.2, 166.56) * mm, "mid": v(94.05, 185.88) * mm, "end": v(37.9, 166.56) * mm});
            skArc(sketch, "E79.11", {"start": v(154.05, 158.68) * mm, "mid": v(153.04, 163.06) * mm, "end": v(150.2, 166.56) * mm});
            skLineSegment(sketch, "E79.12", {"start": v(154.05, 158.68) * mm, "end": v(154.05, 78.09) * mm});
            skArc(sketch, "E79.13", {"start": v(150.2, 70.2) * mm, "mid": v(153.04, 73.7) * mm, "end": v(154.05, 78.09) * mm});
            skArc(sketch, "E79.14", {"start": v(37.9, 70.2) * mm, "mid": v(94.05, 50.88) * mm, "end": v(150.2, 70.2) * mm});
            skArc(sketch, "E79.15", {"start": v(34.05, 78.09) * mm, "mid": v(35.06, 73.7) * mm, "end": v(37.9, 70.2) * mm});
            skLineSegment(sketch, "E80", {"start": v(94.05, 208.38) * mm, "end": v(94.05, 238.38) * mm, "construction": true});
            skCircle(sketch, "E81", {"center": v(94.05, 238.38) * mm, "radius": 6 * mm});
            skLineSegment(sketch, "E82", {"start": v(79.05, 226.38) * mm, "end": v(79.05, 238.38) * mm});
            skLineSegment(sketch, "E83", {"start": v(109.05, 226.38) * mm, "end": v(109.05, 238.38) * mm});
            skArc(sketch, "E84", {"start": v(109.05, 238.38) * mm, "mid": v(94.05, 253.38) * mm, "end": v(79.05, 238.38) * mm});
            skLineSegment(sketch, "E85", {"start": v(79.05, 226.38) * mm, "end": v(61.05, 208.38) * mm});
            skLineSegment(sketch, "E86", {"start": v(109.05, 226.38) * mm, "end": v(127.05, 208.38) * mm});
            skLineSegment(sketch, "E87", {"start": v(14.05, 118.38) * mm, "end": v(174.05, 118.38) * mm, "construction": true});
            skLineSegment(sketch, "E88.MirrorCS", {"start": v(79.05, 10.38) * mm, "end": v(79.05, -1.62) * mm});
            skArc(sketch, "E89.MirrorCS", {"start": v(109.05, -1.62) * mm, "mid": v(94.05, -16.62) * mm, "end": v(79.05, -1.62) * mm});
            skLineSegment(sketch, "E90.MirrorCS", {"start": v(109.05, 10.38) * mm, "end": v(109.05, -1.62) * mm});
            skCircle(sketch, "E91.MirrorC", {"center": v(94.05, -1.62) * mm, "radius": 6 * mm});
            skLineSegment(sketch, "E92.MirrorCS", {"start": v(79.05, 10.38) * mm, "end": v(61.05, 28.38) * mm});
            skLineSegment(sketch, "E93.MirrorCS", {"start": v(94.05, 28.38) * mm, "end": v(94.05, -1.62) * mm, "construction": true});
            skLineSegment(sketch, "E94.MirrorCS", {"start": v(109.05, 10.38) * mm, "end": v(127.05, 28.38) * mm});
            skSolve(sketch);
        }
        {
            var Q0;
            Q0 = qSketchRegion(id + "F16", true);
            var Q1;
            Q1=makeQuery(id+"F2.opExtrude","CAP_FACE",FACE,{"disambiguationData":[OSD([sQuery(id+"F0.wireOp",EDGE,"E12"),sQuery(id+"F0.wireOp",EDGE,"E13"),sQuery(id+"F0.wireOp",EDGE,"E14"),sQuery(id+"F0.wireOp",EDGE,"E15"),sQuery(id+"F0.wireOp",EDGE,"E17.filletArc"),sQuery(id+"F0.wireOp",EDGE,"E18.filletArc"),sQuery(id+"F0.wireOp",EDGE,"E19.filletArc"),sQuery(id+"F0.wireOp",EDGE,"E20.filletArc"),sQuery(id+"F0.wireOp",EDGE,"E25.0"),sQuery(id+"F0.wireOp",EDGE,"E25.1"),sQuery(id+"F0.wireOp",EDGE,"E25.2"),sQuery(id+"F0.wireOp",EDGE,"E25.3"),sQuery(id+"F0.wireOp",EDGE,"E25.4"),sQuery(id+"F0.wireOp",EDGE,"E25.5"),sQuery(id+"F0.wireOp",EDGE,"E25.6"),sQuery(id+"F0.wireOp",EDGE,"E25.7")])],"isStart":false});
            extrude(context, id + "F17", {"entities" : qUnion([Q0]), "operationType" : NewBodyOperationType.ADD, "endBound" : BoundingType.UP_TO_SURFACE, "endBoundEntityFace" : qUnion([Q1]), "depth" : 25 * mm});
        }
    });
